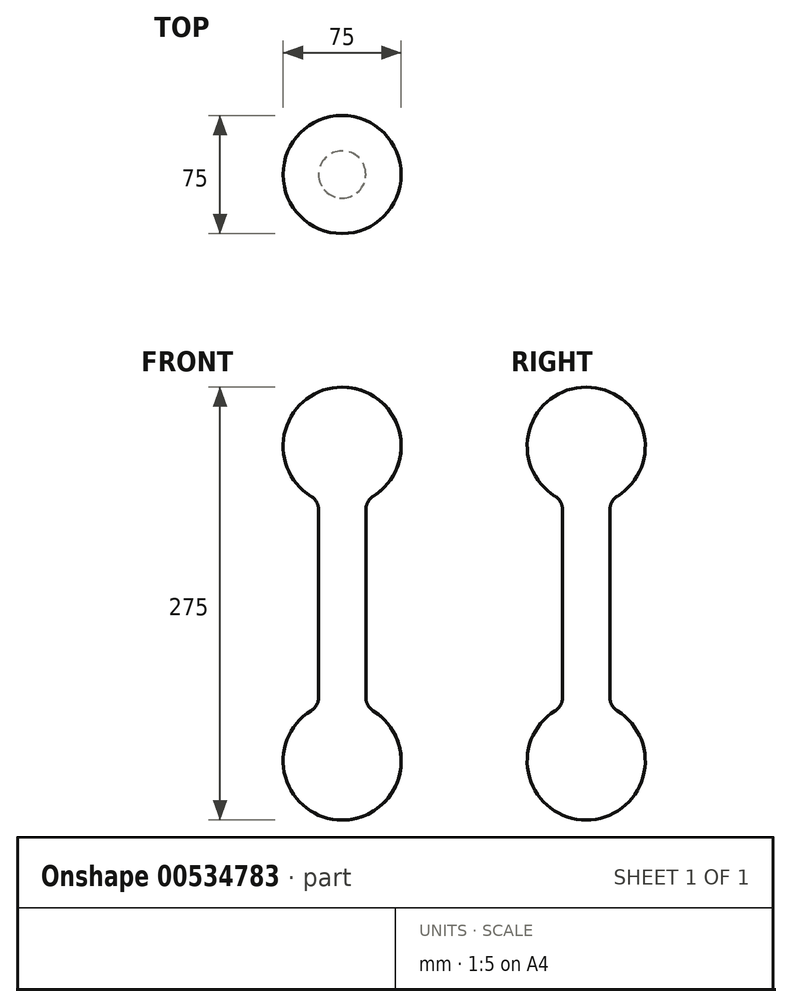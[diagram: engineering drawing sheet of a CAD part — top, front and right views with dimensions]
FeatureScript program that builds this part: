
annotation { "Feature Type Name" : "Feature", "Feature Type Description" : "" }
export const myFeature = defineFeature(function(context is Context, id is Id, definition is map)
    precondition{}
    {
        {
            var Q0;
            Q0=qCreatedBy(makeId("Front.planeOp"),FACE);
            var sketch = newSketch(context, id + "F0", { "sketchPlane" : qUnion([Q0])});
            skLineSegment(sketch, "E0", {"start": v(0, 0) * mm, "end": v(0, 200) * mm});
            skLineSegment(sketch, "E1", {"start": v(0, 200) * mm, "end": v(0, 237.5) * mm});
            skLineSegment(sketch, "E2", {"start": v(0, 0) * mm, "end": v(0, -37.5) * mm});
            skArc(sketch, "E3", {"start": v(0, 237.5) * mm, "mid": v(37.5, 200) * mm, "end": v(0, 162.5) * mm});
            skArc(sketch, "E4", {"start": v(0, -37.5) * mm, "mid": v(37.5, 0) * mm, "end": v(0, 37.5) * mm});
            skLineSegment(sketch, "E5", {"start": v(15, 34.37) * mm, "end": v(15, 165.63) * mm});
            skSolve(sketch);
        }
        {
            var Q0;
            Q0 = qSketchRegion(id + "F0", true);
            var Q1;
            Q1=sQuery(id+"F0.wireOp",EDGE,"E0");
            revolve(context, id + "F1", {"entities" : qUnion([Q0]), "axis" : qUnion([Q1]), "revolveType" : RevolveType.FULL});
        }
        {
            var Q0;
            Q0=makeQuery(id+"F1.opRevolve","SWEPT_FACE",FACE,{"disambiguationData":[OSD([sQuery(id+"F0.wireOp",EDGE,"E5")])]});
            fillet(context, id + "F2", {"entities" : qUnion([Q0]), "radius" : 10 * mm, "tangentPropagation" : true, "allowEdgeOverflow" : false});
        }
    });
